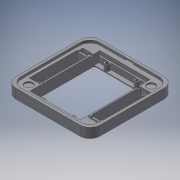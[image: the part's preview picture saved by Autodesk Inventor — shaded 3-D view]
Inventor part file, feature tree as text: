
AUTODESK INVENTOR PART (.ipt)
format: ipt  version: 2016 SP2 (Build 200236200, 236)  size: 443,392 bytes
history: native  units: mm
features: extrude x11, sketch x11, fillet x1, chamfer x1
ambient origin geometry x8: Origin, YZ Plane, XZ Plane, XY Plane, X Axis, Y Axis, Z Axis, Center Point
bodies: Volumenkörper1 (feature_tree)
feature tree (24):
  extrude  "Extrusion1"  Depth=70.3mm
  extrude  "Extrusion2"  Depth=5.0mm
  extrude  "Extrusion7"  Depth=10.5mm
  extrude  "Extrusion8"  Depth=48.3mm
  extrude  "Extrusion9"  Depth=1.2mm
  extrude  "Extrusion10"  Depth=0.8mm
  extrude  "Extrusion12"  Depth=3.0mm
  extrude  "Extrusion13"  Depth=2.0mm
  extrude  "Extrusion14"  Depth=0.5mm
  extrude  "Extrusion15"  Depth=0.8mm
  fillet  "Rundung1"  Radius=0.5mm
  chamfer  "Fase3"  Distance=3.75mm
  extrude  "Extrusion17"  Depth=2.0mm
  sketch  "Skizze1"  dims[d0=50.3mm d1=70.3mm]
  sketch  "Skizze2"  dims[d2=5.0mm d3=5.0mm]
  sketch  "Skizze7"  dims[d4=10.5mm d5=10.5mm]
  sketch  "Skizze8"  dims[d6=48.3mm d7=48.3mm]
  sketch  "Skizze9"  dims[d8=1.2mm d9=1.2mm]
  sketch  "Skizze10"  dims[d11=0.8mm d12=0.8mm]
  sketch  "Skizze12"  dims[d13=0.8mm d14=3.0mm]
  sketch  "Skizze13"  dims[d15=3.75mm d16=2.0mm]
  sketch  "Skizze14"  dims[d17=3.0mm d18=0.5mm]
  sketch  "Skizze15"  dims[d19=0.5mm d20=0.8mm d21=0.5mm d22=0.5mm]
  sketch  "Skizze17"  dims[d23=3.0mm d26=3.75mm d27=2.0mm d28=0.5mm d30=3.0mm d31=0.8mm d32=0.8mm d33=1.6mm d34=1.0mm d35=1.0mm d36=3.0mm d37=3.0mm d38=1.0mm d39=1.0mm d40=1.6mm d41=10.0mm d42=0.0mm d44=59.0mm d45=2.0mm d46=0.8mm d47=0.0mm d80=8.15mm d81=8.15mm d82=6.0mm d83=6.0mm d84=6.0mm d85=6.0mm d86=1.4mm d87=0.0mm d88=3.0mm d89=3.0mm d90=3.8mm d91=0.0mm d92=3.0mm d93=3.0mm d94=3.8mm d95=0.0mm d96=8.5mm d97=0.5mm d98=0.5mm d99=2.0mm d100=0.5mm d101=2.0mm d102=0.5mm d103=1.6mm d104=8.5mm d105=2.0mm d106=0.5mm d107=1.5mm d108=0.0mm d122=2.6mm d123=0.0mm d124=1.9mm d125=0.6mm d126=5.2mm d127=1.0mm d128=5.2mm d129=1.0mm d130=1.2mm d131=0.0mm d132=4.1mm d133=1.0mm d134=8.2mm d135=1.2mm d136=0.0mm d137=10.8mm d138=0.0mm d139=10.0mm d140=5.3mm d141=1.2mm d142=6.108652mm d147=29.5mm d150=1.4mm d151=1.3mm d152=5.0mm d153=3.0mm d154=3.0mm d155=5.0mm d156=3.0mm d157=5.0mm d158=3.0mm d159=5.0mm d160=2.95mm d161=2.95mm d162=15.0mm d163=15.0mm d164=6.0mm d165=0.0mm]
